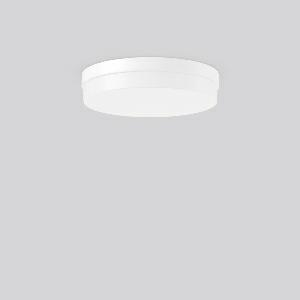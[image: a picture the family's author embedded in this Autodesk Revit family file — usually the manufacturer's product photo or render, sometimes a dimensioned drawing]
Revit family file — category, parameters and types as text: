
# Revit family: flat_kreis_221156_002_8870
name_source: partatom
category: Lighting Fixtures
units: mm (PartAtom-declared; Revit-internal decimal feet)

## family parameters
Cut with Voids When Loaded = No
Host = Face
Light Source = No
Part Type = Normal
Room Calculation Point = No
Round Connector Dimension = Use Diameter
Shared = No

## types (1)
- FLAT KREIS (1 x LED Modul 830, 1200 lm, 3000)
    Apparent Load = 19 VA
    CIE Flux Codes = 42 73 92 91 100
    Color Rendering = 80
    Color Temperature = 3000
    Default Elevation = 1800 mm
    Description = Series: FLAT KREIS
Decorative round surface-mounted luminaire. Base: plastic. Diffuser: plastic (polypropylene), opal. Diffuser fastening: spring system. Homogeneous and smooth light distribution. 
Colour: white
Diameter: 380 mm
Height: 78 mm
Lamp: LED exchangeable
Socket: without socket
Colour temperature: 3000K
Colour rendering index (CRI): 80
System power: 19 W
Rated luminous flux: 1200 lm
Beam angle Down: 121°
Luminous efficiency: 63 lm/W
Control gear: AC Strom, dim.Ph.an-/abschnitt
Protection class: I
Type of protection: IP 43
    Height = 78 mm  [stored 0.255906 ft]
    Lamp = 1 x LED Modul 830
    Lamp Light Flux = 1200 lm
    Lamp count = 1
    Length = 380 mm
    Lifetime = 50000 h
    Luminous efficacy = 63 lm/W
    Manufacturer = RZB
    ModVariant = No
    Model = 221156.002
    Mounting Place = Ceiling, Wall
    Mounting Type = Surface mounted
    Number of Poles = 1
    OnlyDefault = Yes
    Power Factor = 1
    Product Name = FLAT KREIS
    Product group = Surface mounted ceiling and wall luminaires
    ProductGroupID = 305
    Protection Class = Protection class I
    Protection Degree = IP 43
    RLX_Detail_Level = 1
    RLX_Emergency_Light_Flux = 0 lm
    RLX_Emergency_Type = 0
    RLX_Emergency_Type_DB = No
    RlxData = <blob elided: 12893 chars, md5=caa08366>
    Socket = socket
    Standby Power = 0 W
    System Light Flux = 1200 lm
    System Power = 19 W
    Type Comments = ALEA SPOT
    Type Image = 221062.862.79.jpg
    URL = http://relux.com
    VarID = ---
    Voltage = 230 V
    Voltage Range = 220-240 V
    Weight = 0.00 kg
    Width = 0 mm  [stored 0 ft]

note: [stored X ft] marks values corroborated as IEEE doubles in the binary element streams (Revit-internal decimal feet)

## geometry (parser evidence)
native form markers: Sweep x11
no freeform markers — native parametric forms only
